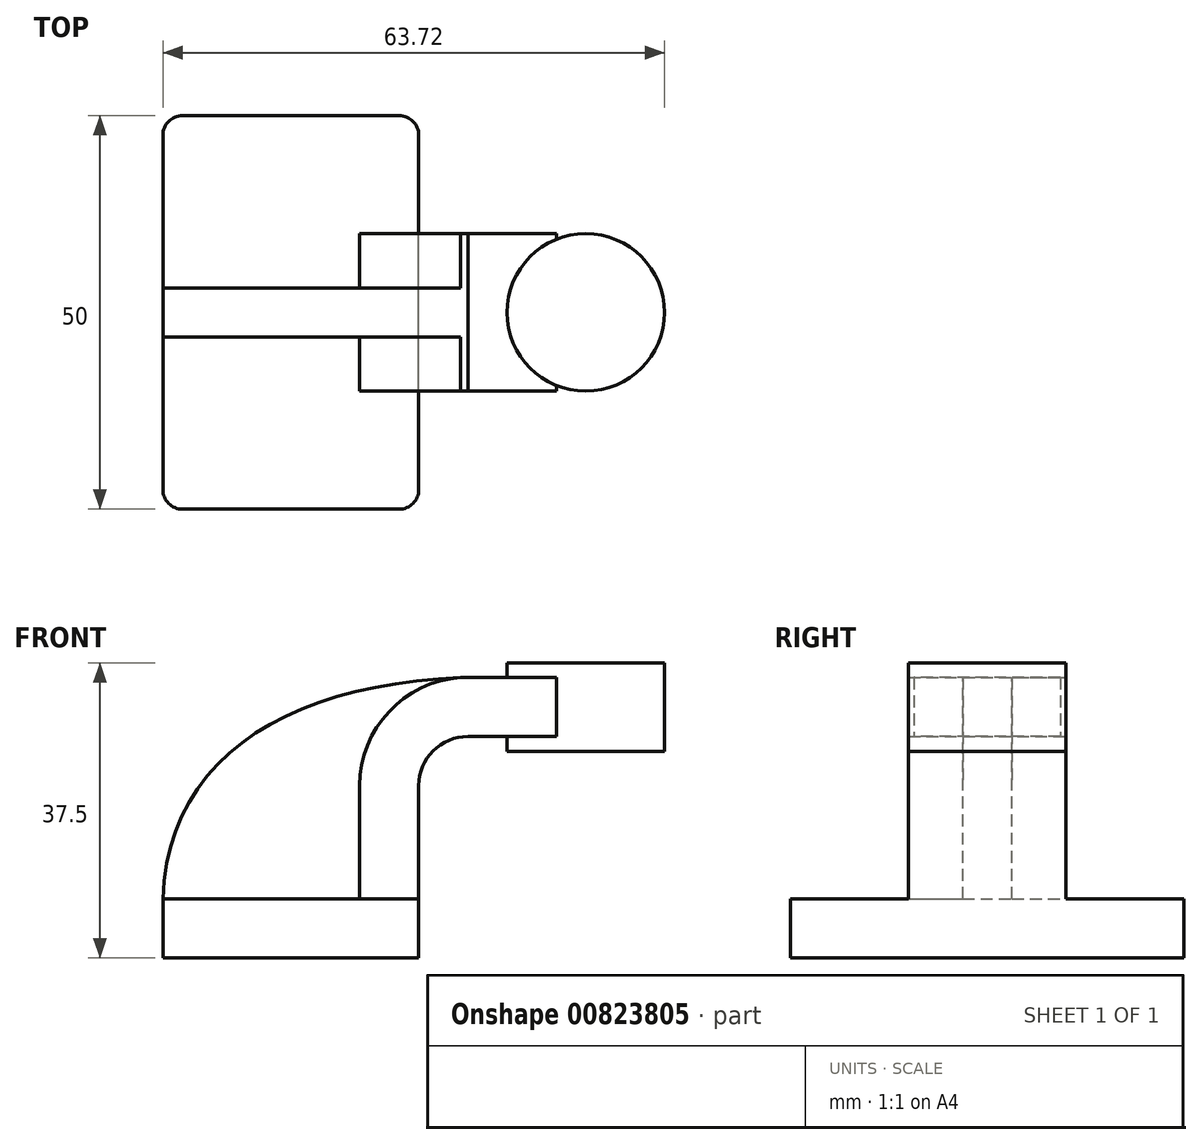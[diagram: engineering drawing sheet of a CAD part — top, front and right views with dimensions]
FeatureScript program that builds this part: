
annotation { "Feature Type Name" : "Feature", "Feature Type Description" : "" }
export const myFeature = defineFeature(function(context is Context, id is Id, definition is map)
    precondition{}
    {
        {
            var Q0;
            Q0=qCreatedBy(makeId("Front.planeOp"),FACE);
            var sketch = newSketch(context, id + "F0", { "sketchPlane" : qUnion([Q0])});
            skLineSegment(sketch, "E0.bottom", {"start": v(16.25, -3.75) * mm, "end": v(-16.25, -3.75) * mm});
            skLineSegment(sketch, "E0.top", {"start": v(16.25, 3.75) * mm, "end": v(-16.25, 3.75) * mm});
            skLineSegment(sketch, "E0.left", {"start": v(16.25, -3.75) * mm, "end": v(16.25, 3.75) * mm});
            skLineSegment(sketch, "E0.right", {"start": v(-16.25, -3.75) * mm, "end": v(-16.25, 3.75) * mm});
            skPoint(sketch, "E0.middle", {"position": v(0, 0) * mm});
            skLineSegment(sketch, "E1", {"start": v(16.25, 3.75) * mm, "end": v(16.25, 18.13) * mm});
            skArc(sketch, "E2", {"start": v(16.25, 18.13) * mm, "mid": v(18.08, 22.55) * mm, "end": v(22.5, 24.38) * mm});
            skLineSegment(sketch, "E3", {"start": v(22.5, 24.38) * mm, "end": v(33.75, 24.38) * mm});
            skLineSegment(sketch, "E4.bottom", {"start": v(27.47, 33.75) * mm, "end": v(47.47, 33.75) * mm});
            skLineSegment(sketch, "E4.top", {"start": v(27.47, 22.5) * mm, "end": v(47.47, 22.5) * mm});
            skLineSegment(sketch, "E4.left", {"start": v(27.47, 33.75) * mm, "end": v(27.47, 22.5) * mm});
            skLineSegment(sketch, "E4.right", {"start": v(47.47, 33.75) * mm, "end": v(47.47, 22.5) * mm});
            skPoint(sketch, "E4.middle", {"position": v(37.47, 28.12) * mm});
            skLineSegment(sketch, "E5.0", {"start": v(22.5, 31.88) * mm, "end": v(33.75, 31.88) * mm});
            skArc(sketch, "E5.1", {"start": v(8.75, 18.13) * mm, "mid": v(12.78, 27.85) * mm, "end": v(22.5, 31.88) * mm});
            skLineSegment(sketch, "E5.2", {"start": v(8.75, 3.75) * mm, "end": v(8.75, 18.13) * mm});
            skLineSegment(sketch, "E6", {"start": v(33.75, 31.88) * mm, "end": v(33.75, 24.38) * mm});
            skFitSpline(sketch, "E7", {"points": [v(-16.25, 3.75) * mm, v(22.5, 31.88) * mm], "startDerivative": vector(1.89, 54.56) * mm, "endDerivative": vector(67.5, 1.9) * mm});
            skLineSegment(sketch, "E8", {"start": v(37.47, 28.12) * mm, "end": v(37.47, 33.75) * mm});
            skLineSegment(sketch, "E9", {"start": v(37.47, 28.12) * mm, "end": v(37.47, 22.5) * mm});
            skSolve(sketch);
        }
        {
            var Q0;
            Q0=makeQuery(id+"F0.imprint","IMPRINT",FACE,{"disambiguationData":[TD([[makeQuery(id+"F0.imprint","IMPRINT",EDGE,{"derivedFrom":sQuery(id+"F0.wireOp",EDGE,"E0.bottom")}),-1.0]])]});
            extrude(context, id + "F1", {"entities" : qUnion([Q0]), "endBound" : BoundingType.SYMMETRIC, "depth" : 50 * mm, "offsetDistance" : 25 * mm});
        }
        {
            var Q0;
            {var subQ4=sQuery(id+"F0.wireOp",EDGE,"E1");Q0=makeQuery(id+"F0.imprint","IMPRINT",FACE,{"disambiguationData":[TD([[makeQuery(id+"F0.imprint","IMPRINT",EDGE,{"derivedFrom":subQ4}),1.0]])]});}
            var Q1;
            {var subQ0=sQuery(id+"F0.wireOp",EDGE,"E6");Q1=makeQuery(id+"F0.imprint","IMPRINT",FACE,{"disambiguationData":[TD([[makeQuery(id+"F0.imprint","IMPRINT",EDGE,{"derivedFrom":subQ0}),-1.0]])]});}
            extrude(context, id + "F2", {"entities" : qUnion([Q0, Q1]), "operationType" : NewBodyOperationType.ADD, "endBound" : BoundingType.SYMMETRIC, "depth" : 20 * mm, "offsetDistance" : 25 * mm});
        }
        {
            var Q0;
            {var subQ3=sQuery(id+"F0.wireOp",EDGE,"E5.2");Q0=makeQuery(id+"F0.imprint","IMPRINT",FACE,{"disambiguationData":[TD([[makeQuery(id+"F0.imprint","IMPRINT",EDGE,{"derivedFrom":subQ3}),1.0]])]});}
            extrude(context, id + "F3", {"entities" : qUnion([Q0]), "operationType" : NewBodyOperationType.ADD, "endBound" : BoundingType.SYMMETRIC, "depth" : 6.25 * mm, "offsetDistance" : 25 * mm});
        }
        {
            var Q0;
            {var subQ0=sQuery(id+"F0.wireOp",EDGE,"E4.right");Q0=makeQuery(id+"F0.imprint","IMPRINT",FACE,{"disambiguationData":[TD([[makeQuery(id+"F0.imprint","IMPRINT",EDGE,{"derivedFrom":subQ0}),-1.0]])]});}
            var Q1;
            Q1=sQuery(id+"F0.wireOp",EDGE,"E8");
            revolve(context, id + "F4", {"operationType" : NewBodyOperationType.ADD, "surfaceOperationType" : NewSurfaceOperationType.NEW, "entities" : qUnion([Q0]), "axis" : qUnion([Q1]), "revolveType" : RevolveType.FULL});
        }
        {
            var Q0;
            Q0=makeQuery(id+"F1.opExtrude","CAP_EDGE",EDGE,{"disambiguationData":[OSD([sQuery(id+"F0.wireOp",EDGE,"E0.left")])],"isStart":false});
            var Q1;
            Q1=makeQuery(id+"F1.opExtrude","CAP_EDGE",EDGE,{"disambiguationData":[OSD([sQuery(id+"F0.wireOp",EDGE,"E0.right")])],"isStart":false});
            var Q2;
            Q2=makeQuery(id+"F1.opExtrude","CAP_EDGE",EDGE,{"disambiguationData":[OSD([sQuery(id+"F0.wireOp",EDGE,"E0.left")])],"isStart":true});
            var Q3;
            Q3=makeQuery(id+"F1.opExtrude","CAP_EDGE",EDGE,{"disambiguationData":[OSD([sQuery(id+"F0.wireOp",EDGE,"E0.right")])],"isStart":true});
            fillet(context, id + "F5", {"entities" : qUnion([Q0, Q1, Q2, Q3]), "radius" : 2.5 * mm, "tangentPropagation" : true, "allowEdgeOverflow" : false});
        }
    });
